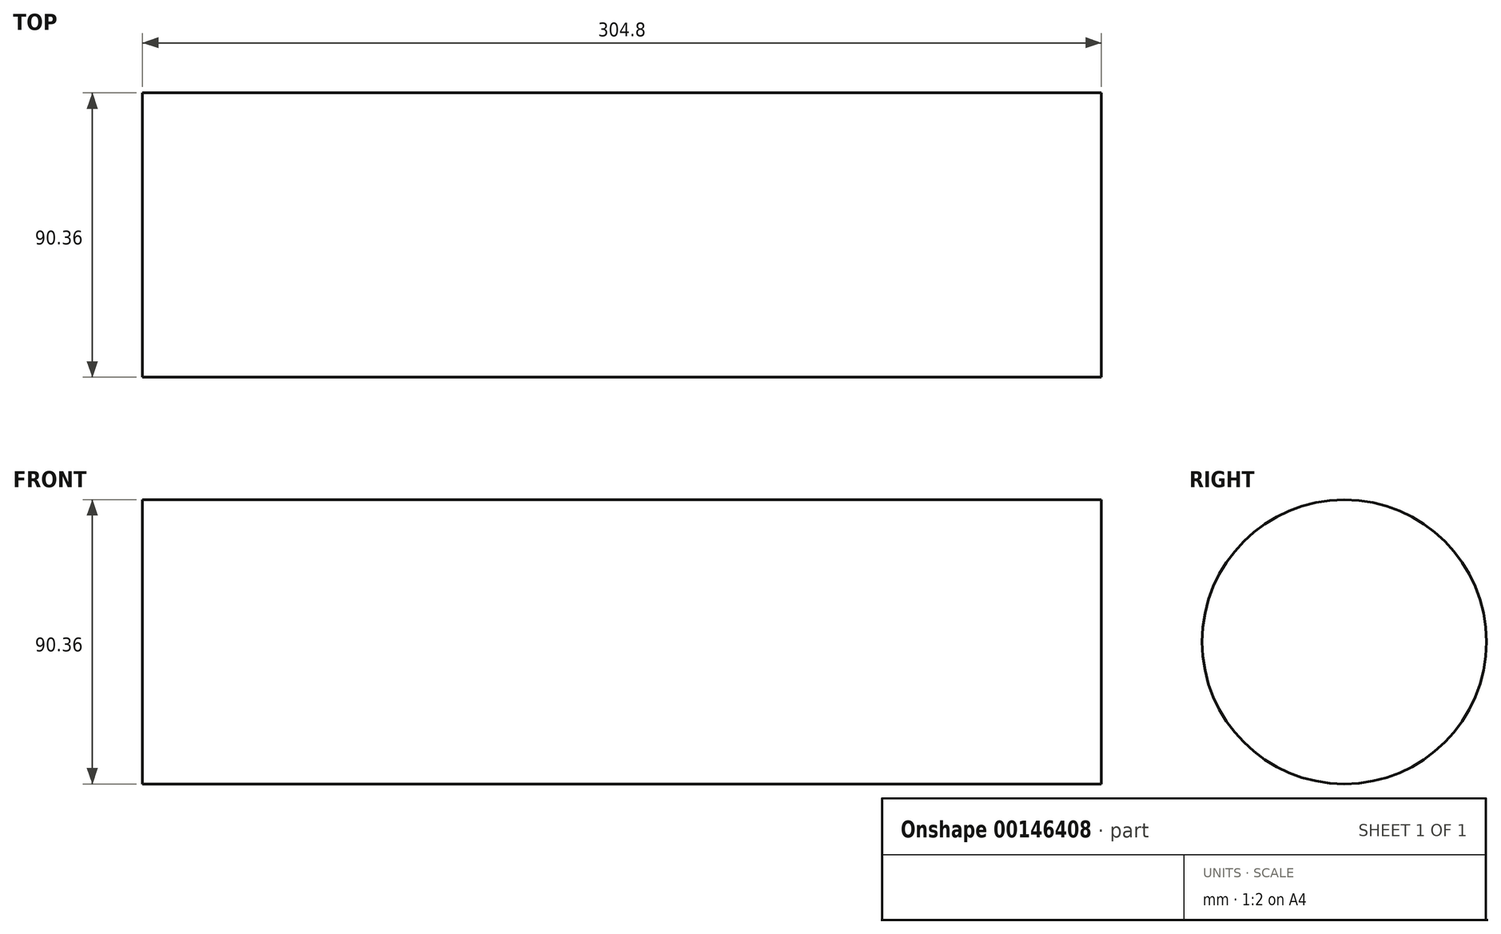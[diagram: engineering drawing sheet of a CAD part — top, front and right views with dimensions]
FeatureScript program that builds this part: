
annotation { "Feature Type Name" : "Feature", "Feature Type Description" : "" }
export const myFeature = defineFeature(function(context is Context, id is Id, definition is map)
    precondition{}
    {
        {
            var Q0;
            Q0=qCreatedBy(makeId("Right.planeOp"),FACE);
            var sketch = newSketch(context, id + "F0", { "sketchPlane" : qUnion([Q0])});
            skCircle(sketch, "E0", {"center": v(0, 0) * mm, "radius": 45.18 * mm});
            skSolve(sketch);
        }
        {
            var Q0;
            Q0 = qSketchRegion(id + "F0", true);
            extrude(context, id + "F1", {"entities" : qUnion([Q0]), "oppositeDirection" : true, "depth" : 304.8 * mm});
        }
    });
